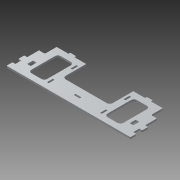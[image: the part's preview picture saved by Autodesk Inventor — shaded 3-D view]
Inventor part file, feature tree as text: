
AUTODESK INVENTOR PART (.ipt)
format: ipt  version: 2013 (Build 170138000, 138)  size: 274,432 bytes
history: native  units: mm
features: extrude x1, sketch x1
ambient origin geometry x8: Origin, YZ Plane, XZ Plane, XY Plane, X Axis, Y Axis, Z Axis, Center Point
feature tree (2):
  extrude  "Extrusion8"  Depth=40.0mm
  sketch  "Sketch1"  dims[d0=80.0mm d1=40.0mm d2=50.0mm d10=50.0mm d15=3.0mm d16=10.0mm d18=10.0mm d20=3.0mm d23=40.0mm d24=40.0mm d27=1.0mm d28=10.0mm d29=6.0mm d31=40.0mm d32=10.0mm d33=6.0mm d35=40.0mm d39=10.0mm d40=3.0mm d41=10.0mm d42=3.0mm d44=10.0mm d45=10.0mm d50=3.0mm d51=10.0mm d52=10.0mm d54=3.0mm d55=10.0mm d56=10.0mm d60=10.0mm d61=3.0mm d62=17.0mm d66=40.0mm d67=40.0mm d71=3.5mm d72=3.5mm d73=3.5mm d74=3.5mm d77=20.0mm d78=20.0mm d79=10.0mm d80=10.0mm d81=2.0mm d82=10.0mm d84=50.0mm d85=20.0mm d86=20.0mm d87=60.0mm d88=5.0mm d92=30.0mm d93=5.0mm d94=30.0mm d95=1.0mm d96=5.0mm d97=10.0mm d98=10.0mm d99=1.0mm d100=10.0mm d101=10.0mm d102=5.0mm d103=5.0mm d104=210.0mm d105=1.0mm d106=5.0mm d107=70.0mm d108=5.0mm d109=27.0mm d110=50.0mm d111=10.0mm d112=12.0mm d113=50.0mm d114=27.0mm d115=12.0mm d116=10.0mm d117=5.0mm d118=3.0mm d119=0.0mm]
